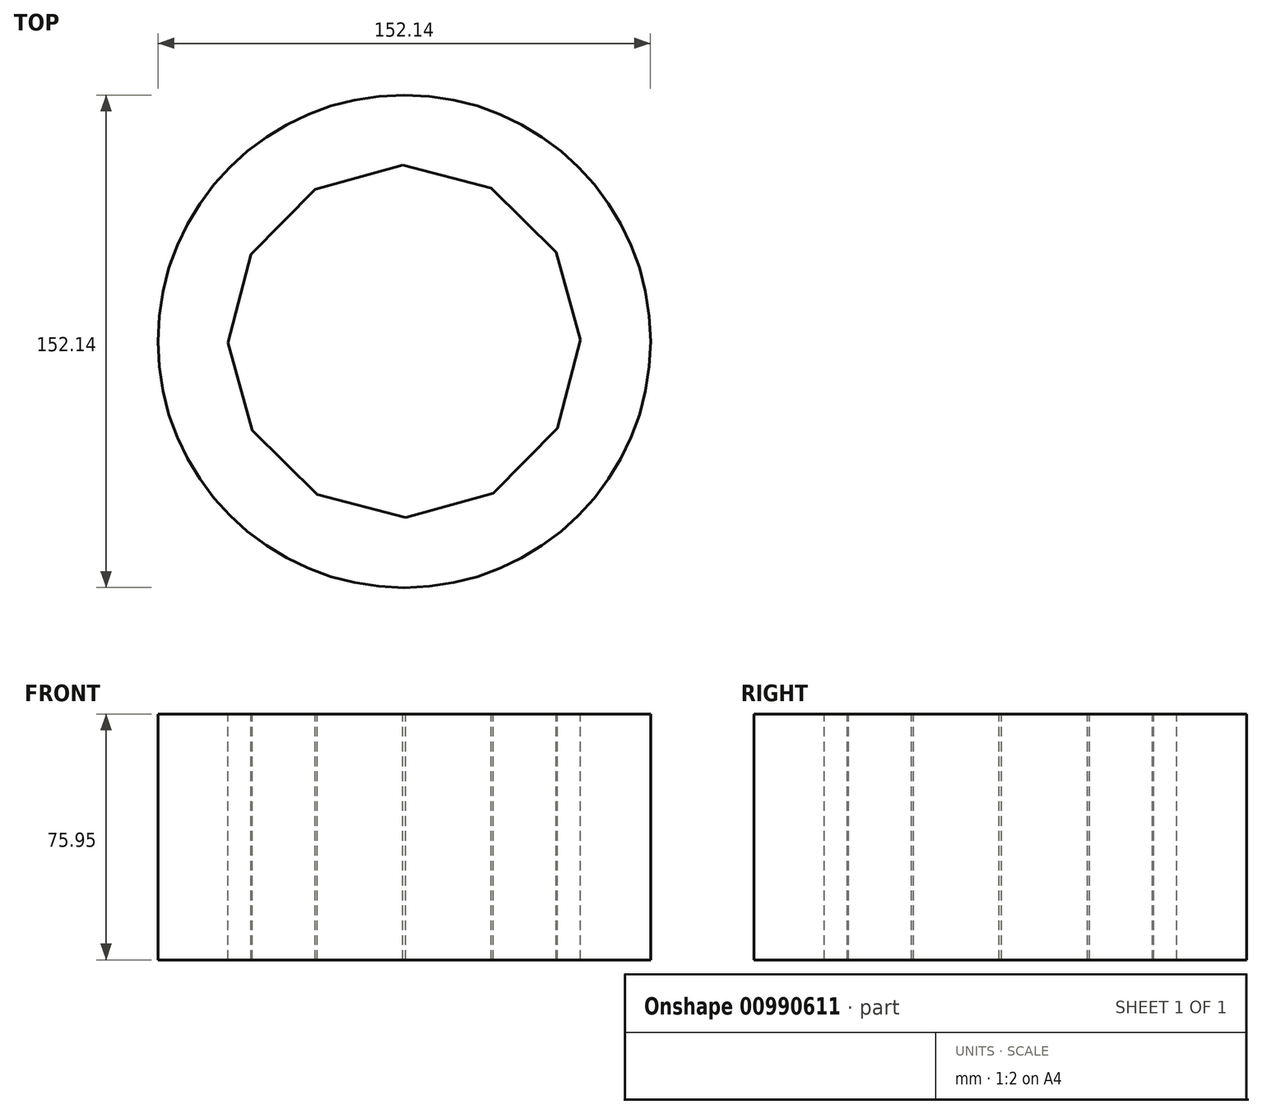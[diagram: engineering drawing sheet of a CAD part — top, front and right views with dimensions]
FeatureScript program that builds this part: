
annotation { "Feature Type Name" : "Feature", "Feature Type Description" : "" }
export const myFeature = defineFeature(function(context is Context, id is Id, definition is map)
    precondition{}
    {
        {
            var Q0;
            Q0=qCreatedBy(makeId("Top.planeOp"),FACE);
            var sketch = newSketch(context, id + "F0", { "sketchPlane" : qUnion([Q0])});
            skCircle(sketch, "E0", {"center": v(0, 0) * mm, "radius": 76.07 * mm});
            skSolve(sketch);
        }
        {
            var Q0;
            Q0 = qSketchRegion(id + "F0", true);
            extrude(context, id + "F1", {"entities" : qUnion([Q0]), "depth" : 75.95 * mm, "offsetDistance" : 25.4 * mm});
        }
        {
            var Q0;
            Q0=makeQuery(id+"F1.opExtrude","CAP_FACE",FACE,{"disambiguationData":[OSD([sQuery(id+"F0.wireOp",EDGE,"E0")])],"isStart":false});
            var sketch = newSketch(context, id + "F2", { "sketchPlane" : qUnion([Q0])});
            skCircle(sketch, "E1.cCircle", {"center": v(0, 0) * mm, "radius": 54.38 * mm, "construction": true});
            skLineSegment(sketch, "E1.0", {"start": v(47.29, -26.85) * mm, "end": v(27.52, -46.9) * mm});
            skLineSegment(sketch, "E1.1", {"start": v(27.52, -46.9) * mm, "end": v(0.39, -54.38) * mm});
            skLineSegment(sketch, "E1.2", {"start": v(0.39, -54.38) * mm, "end": v(-26.85, -47.29) * mm});
            skLineSegment(sketch, "E1.3", {"start": v(-26.85, -47.29) * mm, "end": v(-46.9, -27.52) * mm});
            skLineSegment(sketch, "E1.4", {"start": v(-46.9, -27.52) * mm, "end": v(-54.38, -0.39) * mm});
            skLineSegment(sketch, "E1.5", {"start": v(-54.38, -0.39) * mm, "end": v(-47.29, 26.85) * mm});
            skLineSegment(sketch, "E1.6", {"start": v(-47.29, 26.85) * mm, "end": v(-27.52, 46.9) * mm});
            skLineSegment(sketch, "E1.7", {"start": v(-27.52, 46.9) * mm, "end": v(-0.39, 54.38) * mm});
            skLineSegment(sketch, "E1.8", {"start": v(-0.39, 54.38) * mm, "end": v(26.85, 47.29) * mm});
            skLineSegment(sketch, "E1.9", {"start": v(26.85, 47.29) * mm, "end": v(46.9, 27.52) * mm});
            skLineSegment(sketch, "E1.10", {"start": v(46.9, 27.52) * mm, "end": v(54.38, 0.39) * mm});
            skLineSegment(sketch, "E1.11", {"start": v(54.38, 0.39) * mm, "end": v(47.29, -26.85) * mm});
            skSolve(sketch);
        }
        {
            var Q0;
            Q0=makeQuery(id+"F2.imprint","IMPRINT",FACE,{"disambiguationData":[TD([[makeQuery(id+"F2.imprint","IMPRINT",EDGE,{"derivedFrom":sQuery(id+"F2.wireOp",EDGE,"E1.0")}),-1.0]])]});
            extrude(context, id + "F3", {"entities" : qUnion([Q0]), "operationType" : NewBodyOperationType.REMOVE, "oppositeDirection" : true, "depth" : 149.1 * mm, "offsetDistance" : 25.4 * mm});
        }
    });
